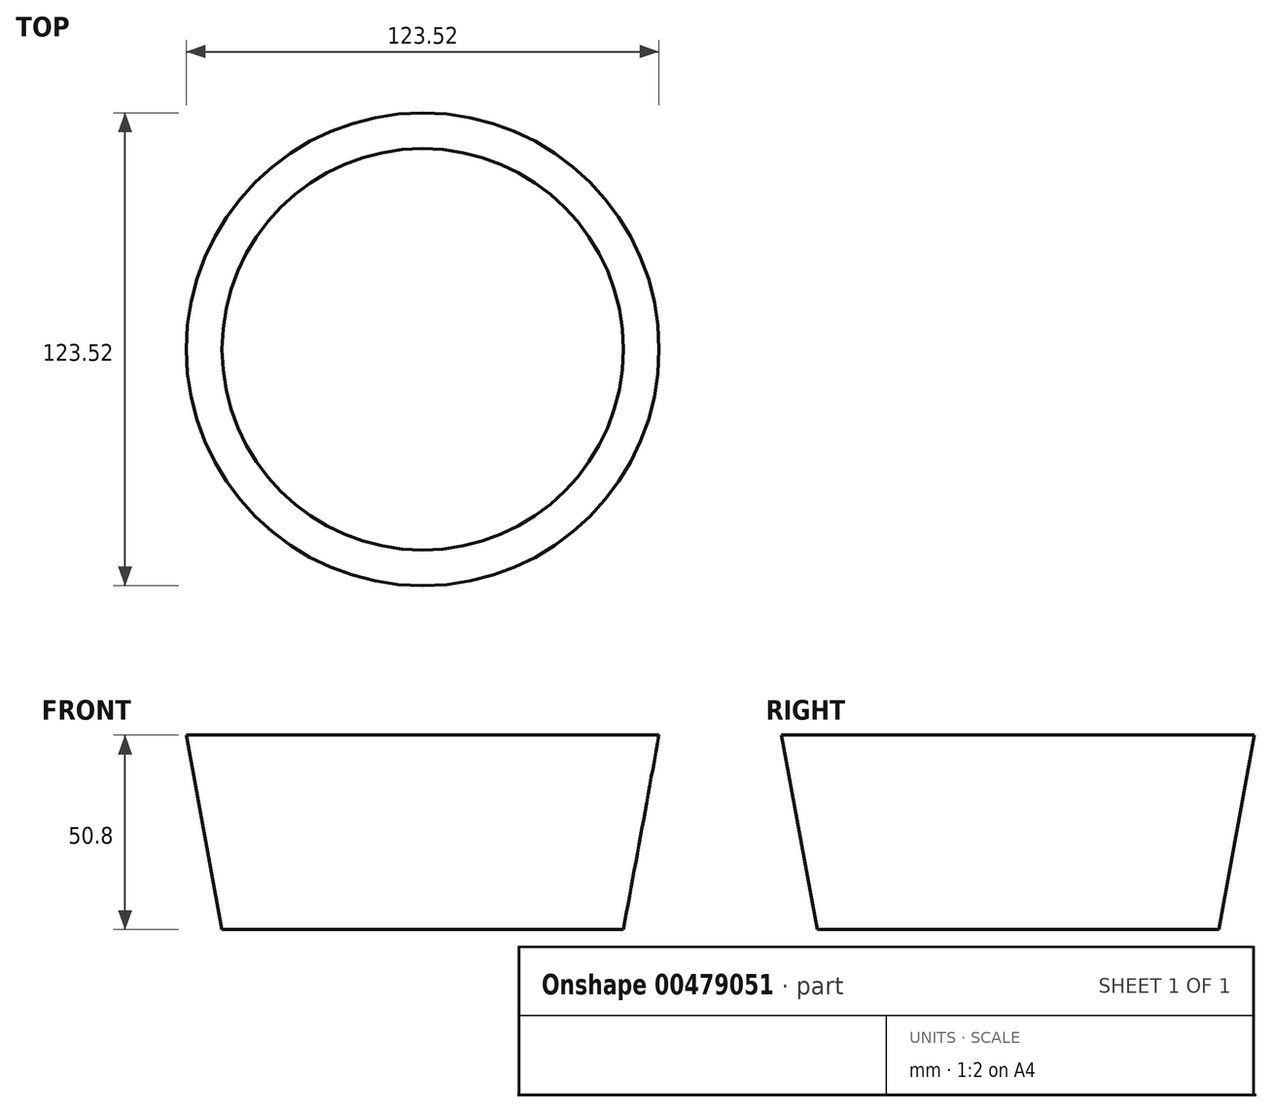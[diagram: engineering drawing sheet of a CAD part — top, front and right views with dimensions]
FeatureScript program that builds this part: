
annotation { "Feature Type Name" : "Feature", "Feature Type Description" : "" }
export const myFeature = defineFeature(function(context is Context, id is Id, definition is map)
    precondition{}
    {
        {
            var Q0;
            Q0=qCreatedBy(makeId("Top.planeOp"),FACE);
            var sketch = newSketch(context, id + "F0", { "sketchPlane" : qUnion([Q0])});
            skCircle(sketch, "E0", {"center": v(0, 0) * mm, "radius": 40 * mm});
            skCircle(sketch, "E1", {"center": v(0, 0) * mm, "radius": 52.42 * mm});
            skSolve(sketch);
        }
        {
            var Q0;
            Q0=qCreatedBy(makeId("Top.planeOp"),FACE);
            cPlane(context, id + "F1", {"entities" : qUnion([Q0]), "cplaneType" : CPlaneType.OFFSET, "offset" : 50.8 * mm, "width" : 152.4 * mm, "height" : 152.4 * mm});
        }
        {
            var Q0;
            Q0=qCreatedBy(id+"F1.planeOp",FACE);
            var sketch = newSketch(context, id + "F2", { "sketchPlane" : qUnion([Q0])});
            skCircle(sketch, "E2", {"center": v(0, 0) * mm, "radius": 49.3 * mm});
            skCircle(sketch, "E3", {"center": v(0, 0) * mm, "radius": 61.76 * mm});
            skSolve(sketch);
        }
        {
            var Q0;
            Q0=sQuery(id+"F0.wireOp",EDGE,"E1");
            var Q1;
            Q1=sQuery(id+"F2.wireOp",EDGE,"E3");
            loft(context, id + "F3", {"bodyType" : ToolBodyType.SURFACE, "wireProfilesArray" : [{ "wireProfileEntities" : qUnion([Q0]) }, { "wireProfileEntities" : qUnion([Q1]) }]});
        }
    });
